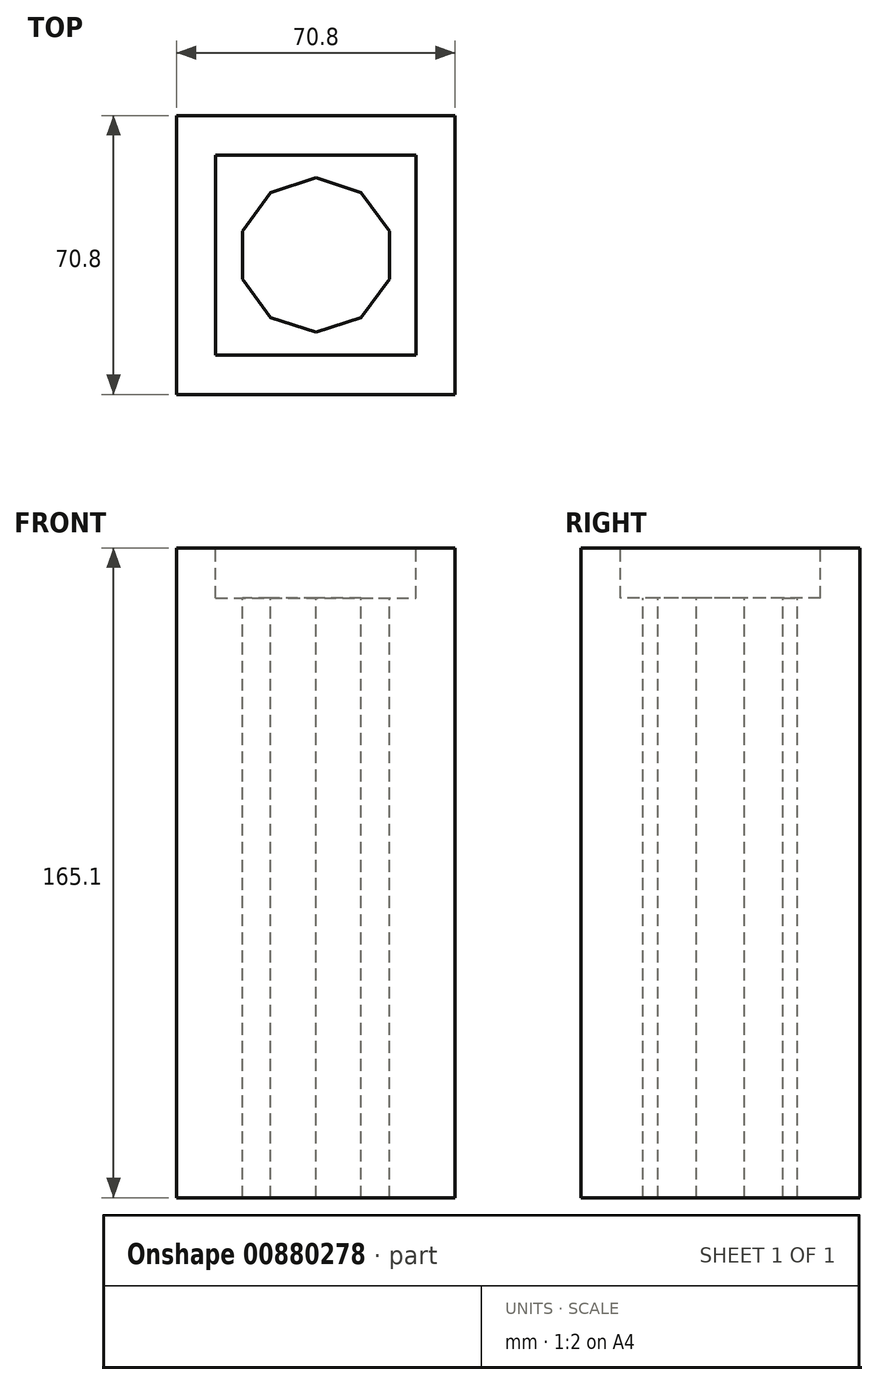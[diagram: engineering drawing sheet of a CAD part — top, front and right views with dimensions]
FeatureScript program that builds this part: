
annotation { "Feature Type Name" : "Feature", "Feature Type Description" : "" }
export const myFeature = defineFeature(function(context is Context, id is Id, definition is map)
    precondition{}
    {
        {
            var Q0;
            Q0=qCreatedBy(makeId("Top.planeOp"),FACE);
            var sketch = newSketch(context, id + "F0", { "sketchPlane" : qUnion([Q0])});
            skLineSegment(sketch, "E0.bottom", {"start": v(-25.4, 25.4) * mm, "end": v(25.4, 25.4) * mm});
            skLineSegment(sketch, "E0.top", {"start": v(-25.4, -25.4) * mm, "end": v(25.4, -25.4) * mm});
            skLineSegment(sketch, "E0.left", {"start": v(-25.4, 25.4) * mm, "end": v(-25.4, -25.4) * mm});
            skLineSegment(sketch, "E0.right", {"start": v(25.4, 25.4) * mm, "end": v(25.4, -25.4) * mm});
            skLineSegment(sketch, "E1.bottom", {"start": v(-35.4, 35.4) * mm, "end": v(35.4, 35.4) * mm});
            skLineSegment(sketch, "E1.top", {"start": v(-35.4, -35.4) * mm, "end": v(35.4, -35.4) * mm});
            skLineSegment(sketch, "E1.left", {"start": v(-35.4, 35.4) * mm, "end": v(-35.4, -35.4) * mm});
            skLineSegment(sketch, "E1.right", {"start": v(35.4, 35.4) * mm, "end": v(35.4, -35.4) * mm});
            skLineSegment(sketch, "E2", {"start": v(0, 25.4) * mm, "end": v(0, -25.4) * mm, "construction": true});
            skSolve(sketch);
        }
        {
            var Q0;
            Q0=makeQuery(id+"F0.imprint","IMPRINT",FACE,{"disambiguationData":[TD([[makeQuery(id+"F0.imprint","IMPRINT",EDGE,{"derivedFrom":sQuery(id+"F0.wireOp",EDGE,"E0.bottom")}),1.0]])]});
            var Q1;
            Q1=makeQuery(id+"F0.imprint","IMPRINT",FACE,{"disambiguationData":[TD([[makeQuery(id+"F0.imprint","IMPRINT",EDGE,{"derivedFrom":sQuery(id+"F0.wireOp",EDGE,"E0.bottom")}),-1.0]])]});
            extrude(context, id + "F1", {"entities" : qUnion([Q0, Q1]), "oppositeDirection" : true, "depth" : 165.1 * mm, "offsetDistance" : 25 * mm});
        }
        {
            var Q0;
            Q0=makeQuery(id+"F0.imprint","IMPRINT",FACE,{"disambiguationData":[TD([[makeQuery(id+"F0.imprint","IMPRINT",EDGE,{"derivedFrom":sQuery(id+"F0.wireOp",EDGE,"E0.bottom")}),-1.0]])]});
            extrude(context, id + "F2", {"entities" : qUnion([Q0]), "operationType" : NewBodyOperationType.REMOVE, "oppositeDirection" : true, "depth" : 12.7 * mm, "offsetDistance" : 25 * mm});
        }
        {
            var Q0;
            Q0=makeQuery(id+"F0.imprint","IMPRINT",FACE,{"disambiguationData":[TD([[makeQuery(id+"F0.imprint","IMPRINT",EDGE,{"derivedFrom":sQuery(id+"F0.wireOp",EDGE,"E0.bottom")}),-1.0]])]});
            var sketch = newSketch(context, id + "F3", { "sketchPlane" : qUnion([Q0])});
            skCircle(sketch, "E3.cCircle", {"center": v(0, 0) * mm, "radius": 18.67 * mm, "construction": true});
            skLineSegment(sketch, "E3.0", {"start": v(18.67, 6.07) * mm, "end": v(18.67, -6.07) * mm});
            skLineSegment(sketch, "E3.1", {"start": v(18.67, -6.07) * mm, "end": v(11.54, -15.88) * mm});
            skLineSegment(sketch, "E3.2", {"start": v(11.54, -15.88) * mm, "end": v(0, -19.63) * mm});
            skLineSegment(sketch, "E3.3", {"start": v(0, -19.63) * mm, "end": v(-11.54, -15.88) * mm});
            skLineSegment(sketch, "E3.4", {"start": v(-11.54, -15.88) * mm, "end": v(-18.67, -6.07) * mm});
            skLineSegment(sketch, "E3.5", {"start": v(-18.67, -6.07) * mm, "end": v(-18.67, 6.07) * mm});
            skLineSegment(sketch, "E3.6", {"start": v(-18.67, 6.07) * mm, "end": v(-11.54, 15.88) * mm});
            skLineSegment(sketch, "E3.7", {"start": v(-11.54, 15.88) * mm, "end": v(0, 19.63) * mm});
            skLineSegment(sketch, "E3.8", {"start": v(0, 19.63) * mm, "end": v(11.54, 15.88) * mm});
            skLineSegment(sketch, "E3.9", {"start": v(11.54, 15.88) * mm, "end": v(18.67, 6.07) * mm});
            skPoint(sketch, "E3.0.midPoint", {"position": v(18.67, 0) * mm});
            skSolve(sketch);
        }
        {
            var Q0;
            Q0=makeQuery(id+"F3.imprint","IMPRINT",FACE,{"disambiguationData":[TD([[makeQuery(id+"F3.imprint","IMPRINT",EDGE,{"derivedFrom":sQuery(id+"F3.wireOp",EDGE,"E3.0")}),-1.0]])]});
            extrude(context, id + "F4", {"entities" : qUnion([Q0]), "operationType" : NewBodyOperationType.REMOVE, "oppositeDirection" : true, "depth" : 200.1 * mm, "offsetDistance" : 25 * mm});
        }
    });
